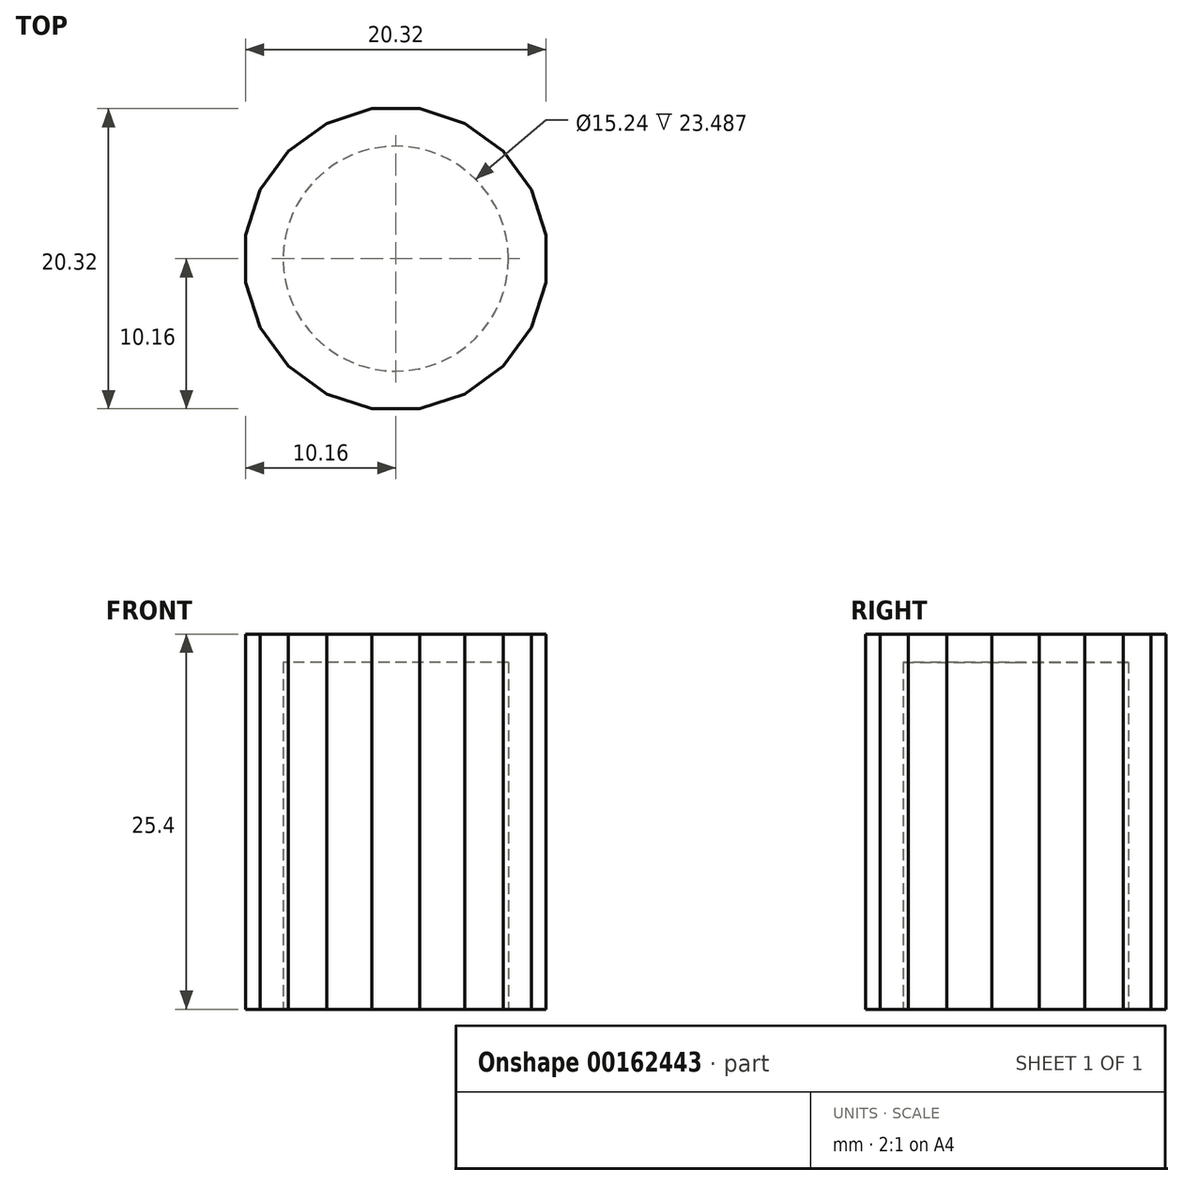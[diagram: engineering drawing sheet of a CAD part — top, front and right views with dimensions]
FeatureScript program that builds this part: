
annotation { "Feature Type Name" : "Feature", "Feature Type Description" : "" }
export const myFeature = defineFeature(function(context is Context, id is Id, definition is map)
    precondition{}
    {
        {
            var Q0;
            Q0=qCreatedBy(makeId("Top.planeOp"),FACE);
            var sketch = newSketch(context, id + "F0", { "sketchPlane" : qUnion([Q0])});
            skCircle(sketch, "E0.cCircle", {"center": v(0, 0) * mm, "radius": 10.16 * mm, "construction": true});
            skLineSegment(sketch, "E0.0", {"start": v(-1.6, 10.16) * mm, "end": v(1.6, 10.16) * mm});
            skLineSegment(sketch, "E0.1", {"start": v(1.6, 10.16) * mm, "end": v(4.67, 9.17) * mm});
            skLineSegment(sketch, "E0.2", {"start": v(4.67, 9.17) * mm, "end": v(7.27, 7.27) * mm});
            skLineSegment(sketch, "E0.3", {"start": v(7.27, 7.27) * mm, "end": v(9.17, 4.67) * mm});
            skLineSegment(sketch, "E0.4", {"start": v(9.17, 4.67) * mm, "end": v(10.16, 1.6) * mm});
            skLineSegment(sketch, "E0.5", {"start": v(10.16, 1.6) * mm, "end": v(10.16, -1.6) * mm});
            skLineSegment(sketch, "E0.6", {"start": v(10.16, -1.6) * mm, "end": v(9.17, -4.67) * mm});
            skLineSegment(sketch, "E0.7", {"start": v(9.17, -4.67) * mm, "end": v(7.27, -7.27) * mm});
            skLineSegment(sketch, "E0.8", {"start": v(7.27, -7.27) * mm, "end": v(4.67, -9.17) * mm});
            skLineSegment(sketch, "E0.9", {"start": v(4.67, -9.17) * mm, "end": v(1.6, -10.16) * mm});
            skLineSegment(sketch, "E0.10", {"start": v(1.6, -10.16) * mm, "end": v(-1.6, -10.16) * mm});
            skLineSegment(sketch, "E0.11", {"start": v(-1.6, -10.16) * mm, "end": v(-4.67, -9.17) * mm});
            skLineSegment(sketch, "E0.12", {"start": v(-4.67, -9.17) * mm, "end": v(-7.27, -7.27) * mm});
            skLineSegment(sketch, "E0.13", {"start": v(-7.27, -7.27) * mm, "end": v(-9.17, -4.67) * mm});
            skLineSegment(sketch, "E0.14", {"start": v(-9.17, -4.67) * mm, "end": v(-10.16, -1.6) * mm});
            skLineSegment(sketch, "E0.15", {"start": v(-10.16, -1.6) * mm, "end": v(-10.16, 1.6) * mm});
            skLineSegment(sketch, "E0.16", {"start": v(-10.16, 1.6) * mm, "end": v(-9.17, 4.67) * mm});
            skLineSegment(sketch, "E0.17", {"start": v(-9.17, 4.67) * mm, "end": v(-7.27, 7.27) * mm});
            skLineSegment(sketch, "E0.18", {"start": v(-7.27, 7.27) * mm, "end": v(-4.67, 9.17) * mm});
            skLineSegment(sketch, "E0.19", {"start": v(-4.67, 9.17) * mm, "end": v(-1.6, 10.16) * mm});
            skPoint(sketch, "E0.0.midPoint", {"position": v(0, 10.16) * mm});
            skPoint(sketch, "E1.0.midPoint", {"position": v(0, 10.64) * mm});
            skPoint(sketch, "E2.orphan", {"position": v(1.68, 10.64) * mm});
            skPoint(sketch, "E3.orphan", {"position": v(7.61, 7.61) * mm});
            skPoint(sketch, "E1.19.end.orphan", {"position": v(-1.68, 10.64) * mm});
            skCircle(sketch, "E4", {"center": v(0, 0) * mm, "radius": 7.62 * mm});
            skSolve(sketch);
        }
        {
            var Q0;
            Q0 = qSketchRegion(id + "F0", true);
            var Q1;
            Q1=makeQuery(id+"F0.imprint","IMPRINT",FACE,{"disambiguationData":[TD([[makeQuery(id+"F0.imprint","IMPRINT",EDGE,{"derivedFrom":sQuery(id+"F0.wireOp",EDGE,"E0.0")}),-1.0]])]});
            var Q2;
            Q2=makeQuery(id+"F0.imprint","IMPRINT",FACE,{"disambiguationData":[TD([[makeQuery(id+"F0.imprint","IMPRINT",EDGE,{"derivedFrom":sQuery(id+"F0.wireOp",EDGE,"E4")}),1.0]])]});
            extrude(context, id + "F1", {"entities" : qUnion([Q0, Q1, Q2]), "depth" : 25.4 * mm});
        }
        {
            var Q0;
            Q0=makeQuery(id+"F0.imprint","IMPRINT",FACE,{"disambiguationData":[TD([[makeQuery(id+"F0.imprint","IMPRINT",EDGE,{"derivedFrom":sQuery(id+"F0.wireOp",EDGE,"E4")}),1.0]])]});
            var Q1;
            Q1=makeQuery(id+"F1.opExtrude","CAP_FACE",FACE,{"disambiguationData":[OSD([sQuery(id+"F0.wireOp",EDGE,"E0.0"),sQuery(id+"F0.wireOp",EDGE,"E0.1"),sQuery(id+"F0.wireOp",EDGE,"E0.2"),sQuery(id+"F0.wireOp",EDGE,"E0.3"),sQuery(id+"F0.wireOp",EDGE,"E0.4"),sQuery(id+"F0.wireOp",EDGE,"E0.5"),sQuery(id+"F0.wireOp",EDGE,"E0.6"),sQuery(id+"F0.wireOp",EDGE,"E0.7"),sQuery(id+"F0.wireOp",EDGE,"E0.8"),sQuery(id+"F0.wireOp",EDGE,"E0.9"),sQuery(id+"F0.wireOp",EDGE,"E0.10"),sQuery(id+"F0.wireOp",EDGE,"E0.11"),sQuery(id+"F0.wireOp",EDGE,"E0.12"),sQuery(id+"F0.wireOp",EDGE,"E0.13"),sQuery(id+"F0.wireOp",EDGE,"E0.14"),sQuery(id+"F0.wireOp",EDGE,"E0.15"),sQuery(id+"F0.wireOp",EDGE,"E0.16"),sQuery(id+"F0.wireOp",EDGE,"E0.17"),sQuery(id+"F0.wireOp",EDGE,"E0.18"),sQuery(id+"F0.wireOp",EDGE,"E0.19")])],"isStart":false});
            extrude(context, id + "F2", {"entities" : qUnion([Q0]), "operationType" : NewBodyOperationType.REMOVE, "endBoundEntityFace" : qUnion([Q1]), "depth" : 23.49 * mm});
        }
    });
